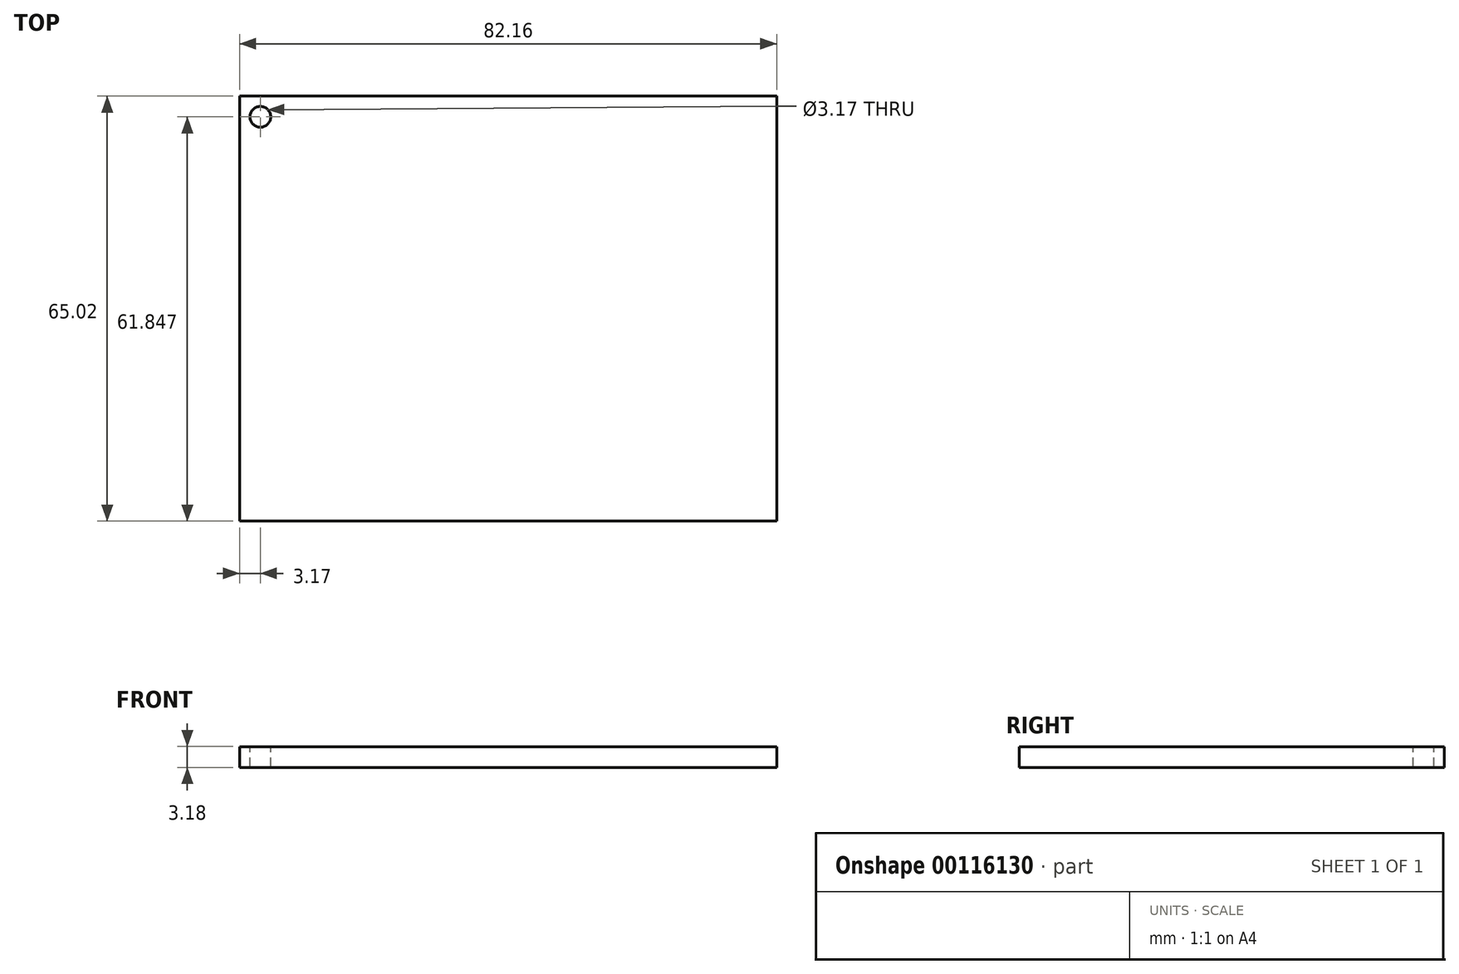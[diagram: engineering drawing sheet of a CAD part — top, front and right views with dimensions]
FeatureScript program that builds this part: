
annotation { "Feature Type Name" : "Feature", "Feature Type Description" : "" }
export const myFeature = defineFeature(function(context is Context, id is Id, definition is map)
    precondition{}
    {
        {
            var Q0;
            Q0=qCreatedBy(makeId("Top.planeOp"),FACE);
            var sketch = newSketch(context, id + "F0", { "sketchPlane" : qUnion([Q0])});
            skLineSegment(sketch, "E0.bottom", {"start": v(41.08, -32.51) * mm, "end": v(-41.08, -32.51) * mm});
            skLineSegment(sketch, "E0.top", {"start": v(41.08, 32.51) * mm, "end": v(-41.08, 32.51) * mm});
            skLineSegment(sketch, "E0.left", {"start": v(41.08, -32.51) * mm, "end": v(41.08, 32.51) * mm});
            skLineSegment(sketch, "E0.right", {"start": v(-41.08, -32.51) * mm, "end": v(-41.08, 32.51) * mm});
            skPoint(sketch, "E0.middle", {"position": v(0, 0) * mm});
            skSolve(sketch);
        }
        {
            var Q0;
            Q0=makeQuery(id+"F0.imprint","IMPRINT",FACE,{"disambiguationData":[TD([[makeQuery(id+"F0.imprint","IMPRINT",EDGE,{"derivedFrom":sQuery(id+"F0.wireOp",EDGE,"E0.bottom")}),-1.0]])]});
            extrude(context, id + "F1", {"entities" : qUnion([Q0]), "depth" : 3.17 * mm});
        }
        {
            var Q0;
            Q0=makeQuery(id+"F1.opExtrude","CAP_FACE",FACE,{"disambiguationData":[OSD([sQuery(id+"F0.wireOp",EDGE,"E0.bottom"),sQuery(id+"F0.wireOp",EDGE,"E0.top"),sQuery(id+"F0.wireOp",EDGE,"E0.left"),sQuery(id+"F0.wireOp",EDGE,"E0.right")])],"isStart":false});
            var sketch = newSketch(context, id + "F2", { "sketchPlane" : qUnion([Q0])});
            skCircle(sketch, "E1", {"center": v(-37.9, 29.34) * mm, "radius": 1.59 * mm});
            skSolve(sketch);
        }
        {
            var Q0;
            Q0 = qSketchRegion(id + "F2", true);
            extrude(context, id + "F3", {"entities" : qUnion([Q0]), "operationType" : NewBodyOperationType.REMOVE, "oppositeDirection" : true, "depth" : 25.4 * mm});
        }
    });
